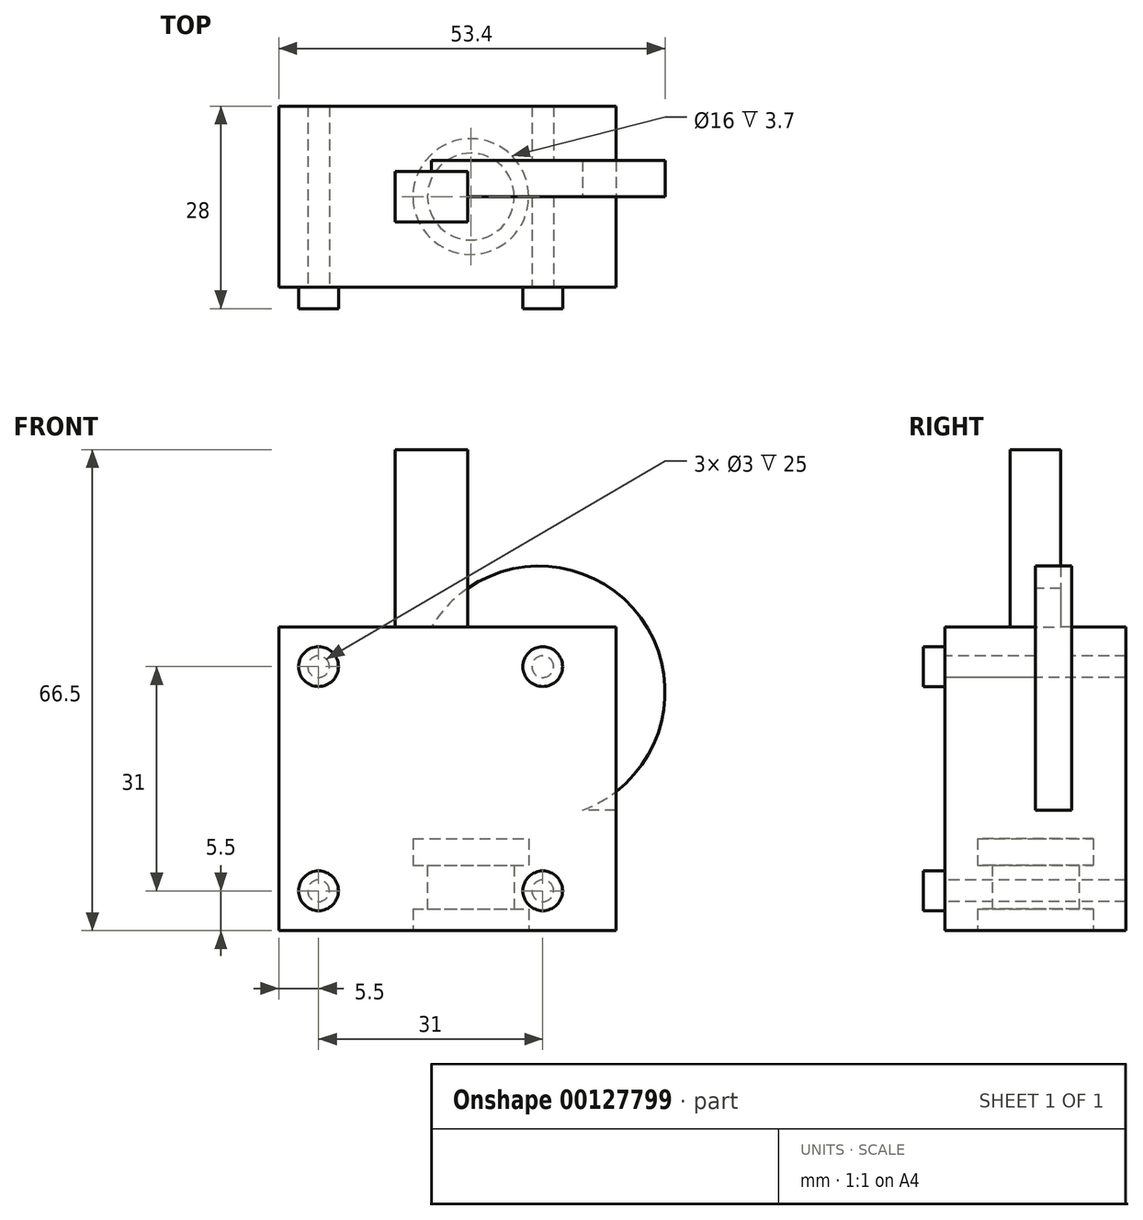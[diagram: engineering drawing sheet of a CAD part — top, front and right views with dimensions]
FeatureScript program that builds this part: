
annotation { "Feature Type Name" : "Feature", "Feature Type Description" : "" }
export const myFeature = defineFeature(function(context is Context, id is Id, definition is map)
    precondition{}
    {
        {
            var Q0;
            Q0=qCreatedBy(makeId("Front.planeOp"),FACE);
            var sketch = newSketch(context, id + "F0", { "sketchPlane" : qUnion([Q0])});
            skLineSegment(sketch, "E0.bottom", {"start": v(21, -21) * mm, "end": v(-21, -21) * mm});
            skLineSegment(sketch, "E0.top", {"start": v(21, 21) * mm, "end": v(-21, 21) * mm});
            skLineSegment(sketch, "E0.left", {"start": v(21, -21) * mm, "end": v(21, 21) * mm});
            skLineSegment(sketch, "E0.right", {"start": v(-21, -21) * mm, "end": v(-21, 21) * mm});
            skPoint(sketch, "E0.middle", {"position": v(0, 0) * mm});
            skSolve(sketch);
        }
        {
            var Q0;
            Q0 = qSketchRegion(id + "F0", true);
            extrude(context, id + "F1", {"entities" : qUnion([Q0]), "endBound" : BoundingType.SYMMETRIC, "depth" : 25 * mm});
        }
        {
            var Q0;
            Q0=makeQuery(id+"F1.opExtrude","CAP_FACE",FACE,{"disambiguationData":[OSD([sQuery(id+"F0.wireOp",EDGE,"E0.bottom"),sQuery(id+"F0.wireOp",EDGE,"E0.top"),sQuery(id+"F0.wireOp",EDGE,"E0.left"),sQuery(id+"F0.wireOp",EDGE,"E0.right")])],"isStart":false});
            var sketch = newSketch(context, id + "F2", { "sketchPlane" : qUnion([Q0])});
            skCircle(sketch, "E1", {"center": v(-15.5, 15.5) * mm, "radius": 1.5 * mm});
            skLineSegment(sketch, "E2", {"start": v(-14.86, 0) * mm, "end": v(0, 0) * mm, "construction": true});
            skLineSegment(sketch, "E3", {"start": v(0, 0) * mm, "end": v(0, 16.85) * mm, "construction": true});
            skPoint(sketch, "E3.endSnap0", {"position": v(0, 21) * mm});
            skCircle(sketch, "E4.MirrorC", {"center": v(15.5, 15.5) * mm, "radius": 1.5 * mm});
            skCircle(sketch, "E5.MirrorC", {"center": v(-15.5, -15.5) * mm, "radius": 1.5 * mm});
            skCircle(sketch, "E6.MirrorC", {"center": v(15.5, -15.5) * mm, "radius": 1.5 * mm});
            skSolve(sketch);
        }
        {
            var Q0;
            Q0 = qSketchRegion(id + "F2", true);
            extrude(context, id + "F3", {"entities" : qUnion([Q0]), "operationType" : NewBodyOperationType.REMOVE, "endBound" : BoundingType.THROUGH_ALL, "oppositeDirection" : true, "depth" : 25 * mm});
        }
        {
            var Q0;
            Q0=qCreatedBy(makeId("Front.planeOp"),FACE);
            var sketch = newSketch(context, id + "F4", { "sketchPlane" : qUnion([Q0])});
            skLineSegment(sketch, "E7", {"start": v(5.55, -8.3) * mm, "end": v(5.55, -21) * mm});
            skLineSegment(sketch, "E8", {"start": v(5.55, -21) * mm, "end": v(13.55, -21) * mm});
            skLineSegment(sketch, "E9", {"start": v(13.55, -21) * mm, "end": v(13.55, -18) * mm});
            skLineSegment(sketch, "E10", {"start": v(13.55, -18) * mm, "end": v(11.55, -18) * mm});
            skLineSegment(sketch, "E11", {"start": v(11.55, -18) * mm, "end": v(11.55, -12) * mm});
            skLineSegment(sketch, "E12", {"start": v(11.55, -12) * mm, "end": v(13.55, -12) * mm});
            skLineSegment(sketch, "E13", {"start": v(13.55, -12) * mm, "end": v(13.55, -8.3) * mm});
            skLineSegment(sketch, "E14", {"start": v(13.55, -8.3) * mm, "end": v(5.55, -8.3) * mm});
            skLineSegment(sketch, "E15", {"start": v(5.55, -21) * mm, "end": v(5.55, -64.52) * mm, "construction": true});
            skSolve(sketch);
        }
        {
            var Q0;
            Q0 = qSketchRegion(id + "F4", true);
            var Q1;
            Q1=sQuery(id+"F4.wireOp",EDGE,"E15");
            revolve(context, id + "F5", {"operationType" : NewBodyOperationType.REMOVE, "entities" : qUnion([Q0]), "axis" : qUnion([Q1]), "revolveType" : RevolveType.FULL, "oppositeDirection" : true});
        }
        {
            var Q0;
            Q0=qCreatedBy(makeId("Front.planeOp"),FACE);
            var sketch = newSketch(context, id + "F6", { "sketchPlane" : qUnion([Q0])});
            skCircle(sketch, "E16", {"center": v(15, 12) * mm, "radius": 17.4 * mm});
            skSolve(sketch);
        }
        {
            var Q0;
            Q0 = qSketchRegion(id + "F6", true);
            extrude(context, id + "F7", {"entities" : qUnion([Q0]), "operationType" : NewBodyOperationType.ADD, "oppositeDirection" : true, "depth" : 5 * mm});
        }
        {
            var Q0;
            Q0=makeQuery(id+"F1.opExtrude","SWEPT_FACE",FACE,{"disambiguationData":[OSD([sQuery(id+"F0.wireOp",EDGE,"E0.left")])]});
            extrude(context, id + "F8", {"entities" : qUnion([Q0]), "operationType" : NewBodyOperationType.ADD, "depth" : 4.6 * mm});
        }
        {
            var Q0;
            {var subQ1=sQuery(id+"F0.wireOp",EDGE,"E0.left");var subQ2=sQuery(id+"F0.wireOp",EDGE,"E0.top");var subQ4=makeQuery(id+"F1.opExtrude","SWEPT_FACE",FACE,{"disambiguationData":[OSD([subQ2])]});var subQ5=sQuery(id+"F6.wireOp",EDGE,"E16");var subQ7=makeQuery(id+"F1.opExtrude","SWEPT_EDGE",EDGE,{"disambiguationData":[OSD([subQ2,subQ1])]});Q0=makeQuery(id+"F8.boolean.opBoolean","MERGE",FACE,{"derivedFrom":[subQ4,makeQuery(id+"F8.opExtrude","SWEPT_FACE",FACE,{"disambiguationData":[OSD([subQ2,subQ1]),TDD([makeQuery(id+"F7.boolean.opBoolean","SPLIT",EDGE,{"disambiguationData":[TD([makeQuery(id+"F7.opExtrude","CAP_FACE",FACE,{"disambiguationData":[OSD([subQ5])],"isStart":false})])],"derivedFrom":subQ7})])]}),makeQuery(id+"F8.opExtrude","SWEPT_FACE",FACE,{"disambiguationData":[OSD([subQ2,subQ1]),TDD([makeQuery(id+"F7.boolean.opBoolean","SPLIT",EDGE,{"disambiguationData":[TD([makeQuery(id+"F7.opExtrude","CAP_FACE",FACE,{"disambiguationData":[OSD([subQ5])],"isStart":true})])],"derivedFrom":subQ7})])]})]});}
            var sketch = newSketch(context, id + "F9", { "sketchPlane" : qUnion([Q0])});
            skLineSegment(sketch, "E17.bottom", {"start": v(5.1, -3.5) * mm, "end": v(-4.9, -3.5) * mm});
            skLineSegment(sketch, "E17.top", {"start": v(5.1, 3.5) * mm, "end": v(-4.9, 3.5) * mm});
            skLineSegment(sketch, "E17.left", {"start": v(5.1, -3.5) * mm, "end": v(5.1, 3.5) * mm});
            skLineSegment(sketch, "E17.right", {"start": v(-4.9, -3.5) * mm, "end": v(-4.9, 3.5) * mm});
            skPoint(sketch, "E17.middle", {"position": v(0.1, 0) * mm});
            skSolve(sketch);
        }
        {
            var Q0;
            Q0 = qSketchRegion(id + "F9", true);
            extrude(context, id + "F10", {"entities" : qUnion([Q0]), "operationType" : NewBodyOperationType.ADD, "depth" : 24.5 * mm});
        }
        {
            var Q0;
            {var subQ0=sQuery(id+"F0.wireOp",EDGE,"E0.left");Q0=makeQuery(id+"F8.boolean.opBoolean","MERGE",FACE,{"derivedFrom":[makeQuery(id+"F1.opExtrude","CAP_FACE",FACE,{"disambiguationData":[OSD([sQuery(id+"F0.wireOp",EDGE,"E0.bottom"),sQuery(id+"F0.wireOp",EDGE,"E0.top"),subQ0,sQuery(id+"F0.wireOp",EDGE,"E0.right")])],"isStart":false}),makeQuery(id+"F8.opExtrude","SWEPT_FACE",FACE,{"disambiguationData":[OSD([subQ0]),TDD([makeQuery(id+"F1.opExtrude","CAP_EDGE",EDGE,{"disambiguationData":[OSD([subQ0])],"isStart":false})])]})]});}
            var sketch = newSketch(context, id + "F11", { "sketchPlane" : qUnion([Q0])});
            skCircle(sketch, "E18", {"center": v(-15.5, 15.5) * mm, "radius": 2.75 * mm});
            skCircle(sketch, "E19", {"center": v(-15.5, -15.5) * mm, "radius": 2.75 * mm});
            skCircle(sketch, "E20", {"center": v(15.5, -15.5) * mm, "radius": 2.75 * mm});
            skCircle(sketch, "E21", {"center": v(15.5, 15.5) * mm, "radius": 2.75 * mm});
            skSolve(sketch);
        }
        {
            var Q0;
            Q0 = qSketchRegion(id + "F11", true);
            extrude(context, id + "F12", {"entities" : qUnion([Q0]), "operationType" : NewBodyOperationType.ADD, "depth" : 3 * mm});
        }
    });
